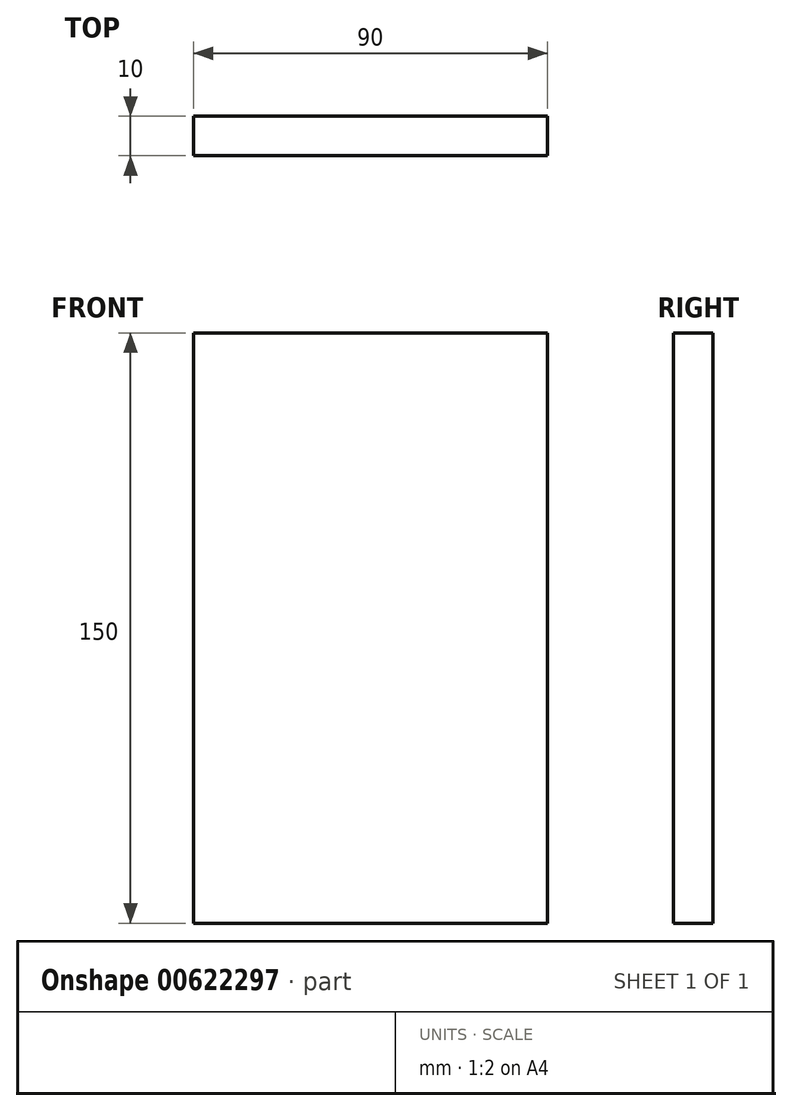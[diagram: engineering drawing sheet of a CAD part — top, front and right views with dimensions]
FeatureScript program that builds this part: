
annotation { "Feature Type Name" : "Feature", "Feature Type Description" : "" }
export const myFeature = defineFeature(function(context is Context, id is Id, definition is map)
    precondition{}
    {
        {
            var Q0;
            Q0=qCreatedBy(makeId("Front.planeOp"),FACE);
            var sketch = newSketch(context, id + "F0", { "sketchPlane" : qUnion([Q0])});
            skLineSegment(sketch, "E0.bottom", {"start": v(-45, 75) * mm, "end": v(45, 75) * mm});
            skLineSegment(sketch, "E0.top", {"start": v(-45, -75) * mm, "end": v(45, -75) * mm});
            skLineSegment(sketch, "E0.left", {"start": v(-45, 75) * mm, "end": v(-45, -75) * mm});
            skLineSegment(sketch, "E0.right", {"start": v(45, 75) * mm, "end": v(45, -75) * mm});
            skPoint(sketch, "E0.middle", {"position": v(0, 0) * mm});
            skSolve(sketch);
        }
        {
            var Q0;
            Q0 = qSketchRegion(id + "F0", true);
            extrude(context, id + "F1", {"entities" : qUnion([Q0]), "depth" : 10 * mm, "offsetDistance" : 25 * mm});
        }
    });
